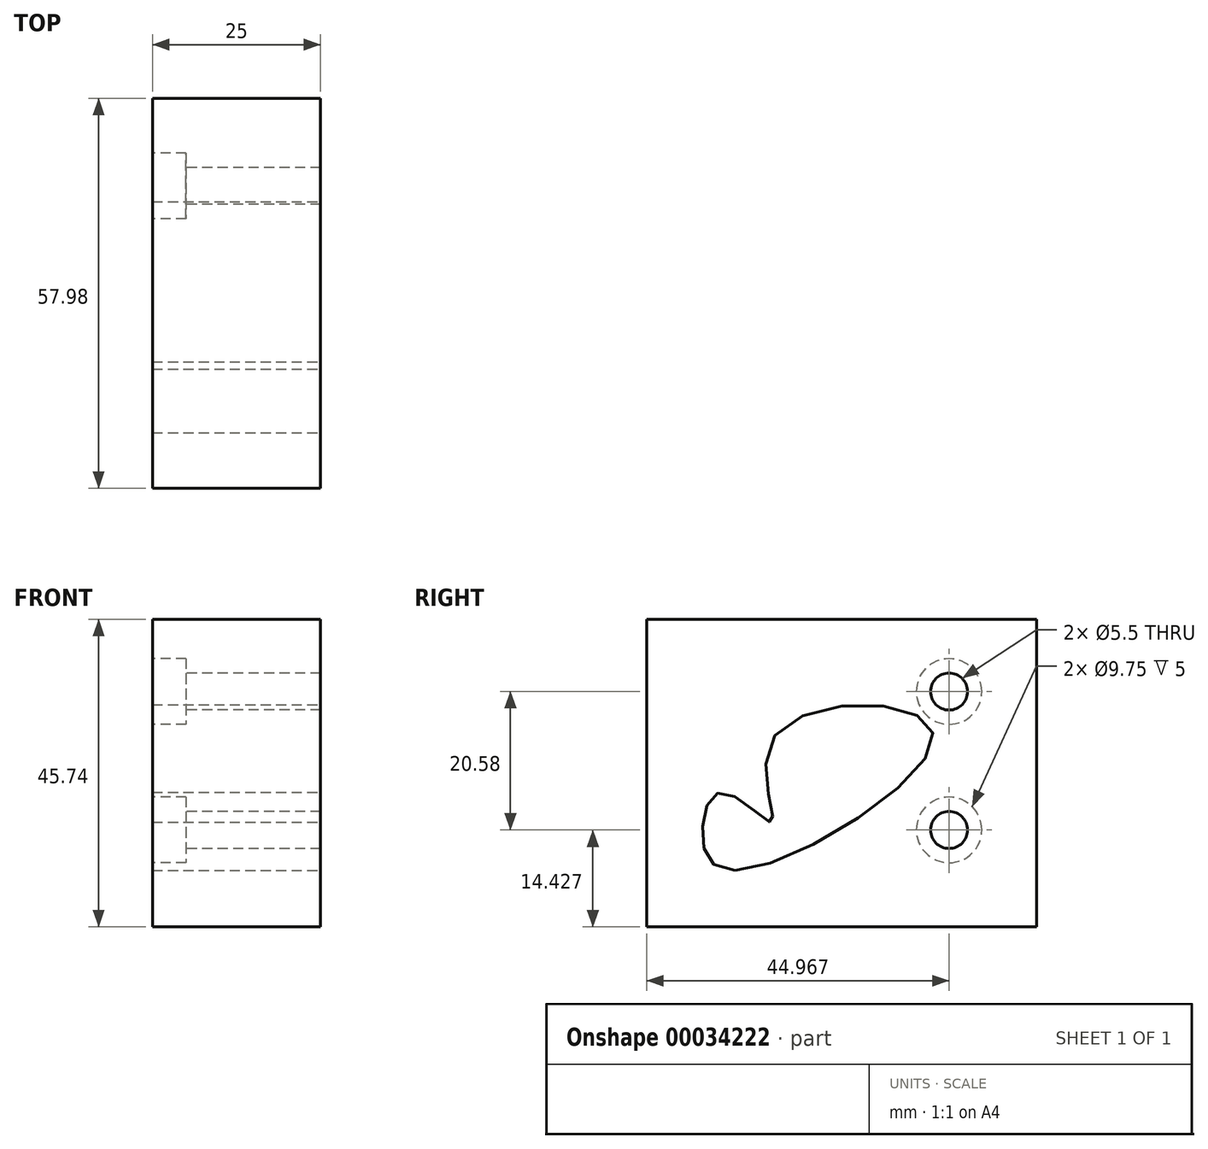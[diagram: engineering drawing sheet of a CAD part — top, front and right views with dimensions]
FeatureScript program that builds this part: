
annotation { "Feature Type Name" : "Feature", "Feature Type Description" : "" }
export const myFeature = defineFeature(function(context is Context, id is Id, definition is map)
    precondition{}
    {
        {
            var Q0;
            Q0=qCreatedBy(makeId("Right.planeOp"),FACE);
            var sketch = newSketch(context, id + "F0", { "sketchPlane" : qUnion([Q0])});
            skLineSegment(sketch, "E0.bottom", {"start": v(28.99, 22.87) * mm, "end": v(-28.99, 22.87) * mm});
            skLineSegment(sketch, "E0.top", {"start": v(28.99, -22.87) * mm, "end": v(-28.99, -22.87) * mm});
            skLineSegment(sketch, "E0.left", {"start": v(28.99, 22.87) * mm, "end": v(28.99, -22.87) * mm});
            skLineSegment(sketch, "E0.right", {"start": v(-28.99, 22.87) * mm, "end": v(-28.99, -22.87) * mm});
            skPoint(sketch, "E0.middle", {"position": v(0, 0) * mm});
            skSolve(sketch);
        }
        {
            var Q0;
            Q0 = qSketchRegion(id + "F0", true);
            extrude(context, id + "F1", {"entities" : qUnion([Q0]), "depth" : 25 * mm});
        }
        {
            var Q0;
            Q0=makeQuery(id+"F1.opExtrude","CAP_FACE",FACE,{"disambiguationData":[OSD([sQuery(id+"F0.wireOp",EDGE,"E0.bottom"),sQuery(id+"F0.wireOp",EDGE,"E0.top"),sQuery(id+"F0.wireOp",EDGE,"E0.left"),sQuery(id+"F0.wireOp",EDGE,"E0.right")])],"isStart":true});
            var sketch = newSketch(context, id + "F2", { "sketchPlane" : qUnion([Q0])});
            skPoint(sketch, "E1", {"position": v(-15.98, 12.14) * mm});
            skPoint(sketch, "E2", {"position": v(-15.98, -8.44) * mm});
            skSolve(sketch);
        }
        {
            var Q0;
            Q0=sQuery(id+"F2.wireOp",VERTEX,"E1");
            var Q1;
            Q1=sQuery(id+"F2.wireOp",VERTEX,"E2");
            var Q2;
            Q2=makeQuery(id+"F1.opExtrude","SWEPT_BODY",BODY,{"disambiguationData":[OSD([sQuery(id+"F0.wireOp",EDGE,"E0.bottom"),sQuery(id+"F0.wireOp",EDGE,"E0.top"),sQuery(id+"F0.wireOp",EDGE,"E0.left"),sQuery(id+"F0.wireOp",EDGE,"E0.right")])]});
            hole(context, id + "F3", {"style" : HoleStyle.C_BORE, "endStyle" : HoleEndStyle.THROUGH, "standardTappedOrClearance" : lookupTablePath({ "standard" : "ISO", "fit" : "Normal", "size" : "M5", "type" : "Clearance" }), "standardBlindInLast" : lookupTablePath({ "fit" : "Standard", "standard" : "ISO", "size" : "M5", "type" : "Clearance" }), "holeDiameter" : 5.5 * mm, "cBoreDiameter" : 9.75 * mm, "cBoreDepth" : 5 * mm, "locations" : qUnion([Q0, Q1]), "scope" : qUnion([Q2]), "isTappedThrough" : true});
        }
        {
            var Q0;
            Q0=makeQuery(id+"F1.opExtrude","CAP_FACE",FACE,{"disambiguationData":[OSD([sQuery(id+"F0.wireOp",EDGE,"E0.bottom"),sQuery(id+"F0.wireOp",EDGE,"E0.top"),sQuery(id+"F0.wireOp",EDGE,"E0.left"),sQuery(id+"F0.wireOp",EDGE,"E0.right")])],"isStart":false});
            var sketch = newSketch(context, id + "F4", { "sketchPlane" : qUnion([Q0])});
            skFitSpline(sketch, "E3", {"points": [v(-15.86, -14.48) * mm, v(-20.72, -8.56) * mm, v(-17.55, -2.85) * mm, v(-10.36, -7.3) * mm, v(-9.94, 5.6) * mm, v(13.53, 6.24) * mm, v(-15.86, -14.48) * mm]});
            skSolve(sketch);
        }
        {
            var Q0;
            Q0=makeQuery(id+"F4.imprint","IMPRINT",FACE,{"disambiguationData":[TD([[makeQuery(id+"F4.imprint","IMPRINT",EDGE,{"derivedFrom":sQuery(id+"F4.wireOp",EDGE,"E3")}),-1.0]])]});
            extrude(context, id + "F5", {"entities" : qUnion([Q0]), "endBound" : BoundingType.UP_TO_NEXT, "oppositeDirection" : true, "depth" : 56.5 * mm});
        }
    });
